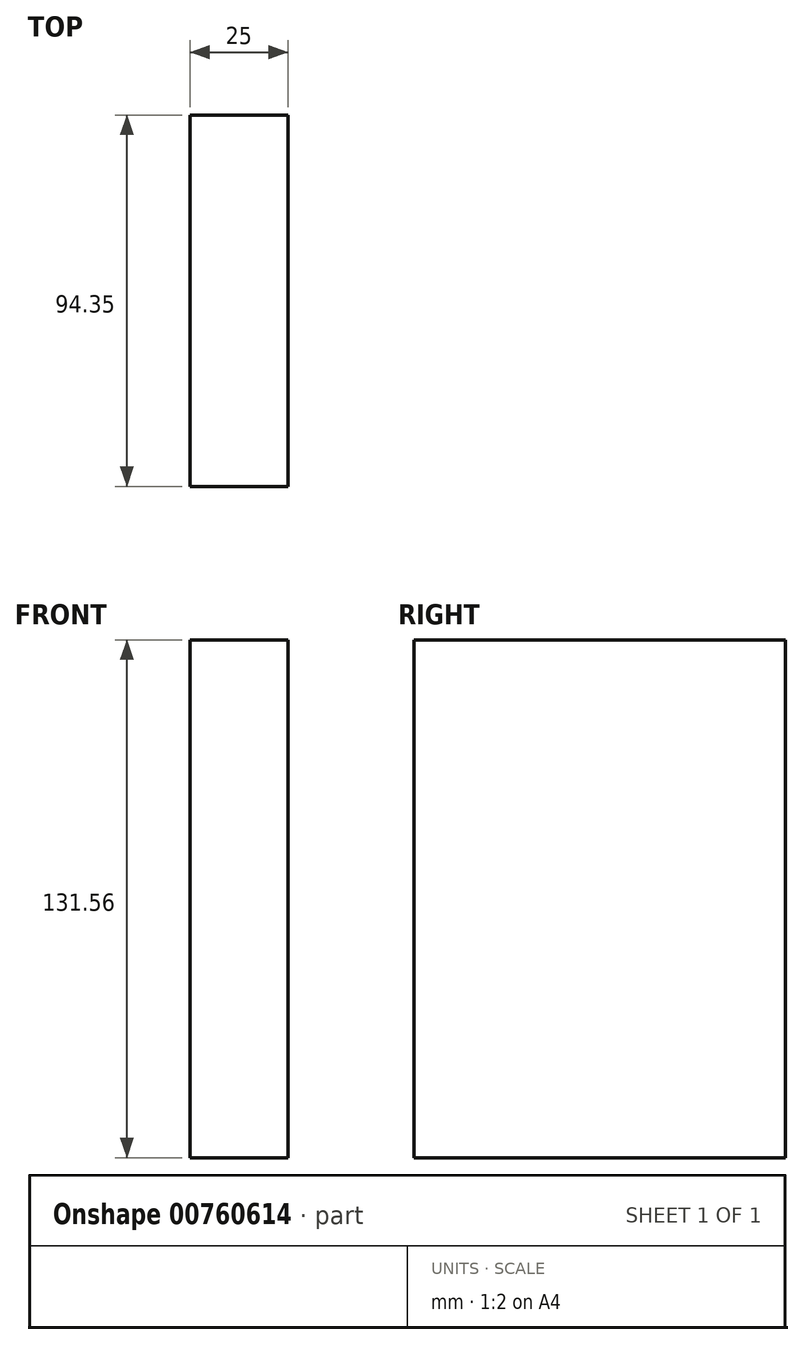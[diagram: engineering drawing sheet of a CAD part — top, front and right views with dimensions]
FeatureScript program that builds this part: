
annotation { "Feature Type Name" : "Feature", "Feature Type Description" : "" }
export const myFeature = defineFeature(function(context is Context, id is Id, definition is map)
    precondition{}
    {
        {
            var Q0;
            Q0=qCreatedBy(makeId("Right.planeOp"),FACE);
            var sketch = newSketch(context, id + "F0", { "sketchPlane" : qUnion([Q0])});
            skLineSegment(sketch, "E0.bottom", {"start": v(19.06, -18.14) * mm, "end": v(113.4, -18.14) * mm});
            skLineSegment(sketch, "E0.top", {"start": v(19.06, -149.7) * mm, "end": v(113.4, -149.7) * mm});
            skLineSegment(sketch, "E0.left", {"start": v(19.06, -18.14) * mm, "end": v(19.06, -149.7) * mm});
            skLineSegment(sketch, "E0.right", {"start": v(113.4, -18.14) * mm, "end": v(113.4, -149.7) * mm});
            skSolve(sketch);
        }
        {
            var Q0;
            Q0=sQuery(id+"F0.wireOp",EDGE,"E0.top");
            var Q1;
            Q1=sQuery(id+"F0.wireOp",EDGE,"E0.right");
            var Q2;
            Q2=sQuery(id+"F0.wireOp",EDGE,"E0.left");
            var Q3;
            Q3=sQuery(id+"F0.wireOp",EDGE,"E0.bottom");
            extrude(context, id + "F1", {"bodyType" : ToolBodyType.SURFACE, "surfaceEntities" : qUnion([Q0, Q1, Q2, Q3]), "depth" : 25 * mm, "offsetDistance" : 25 * mm});
        }
    });
